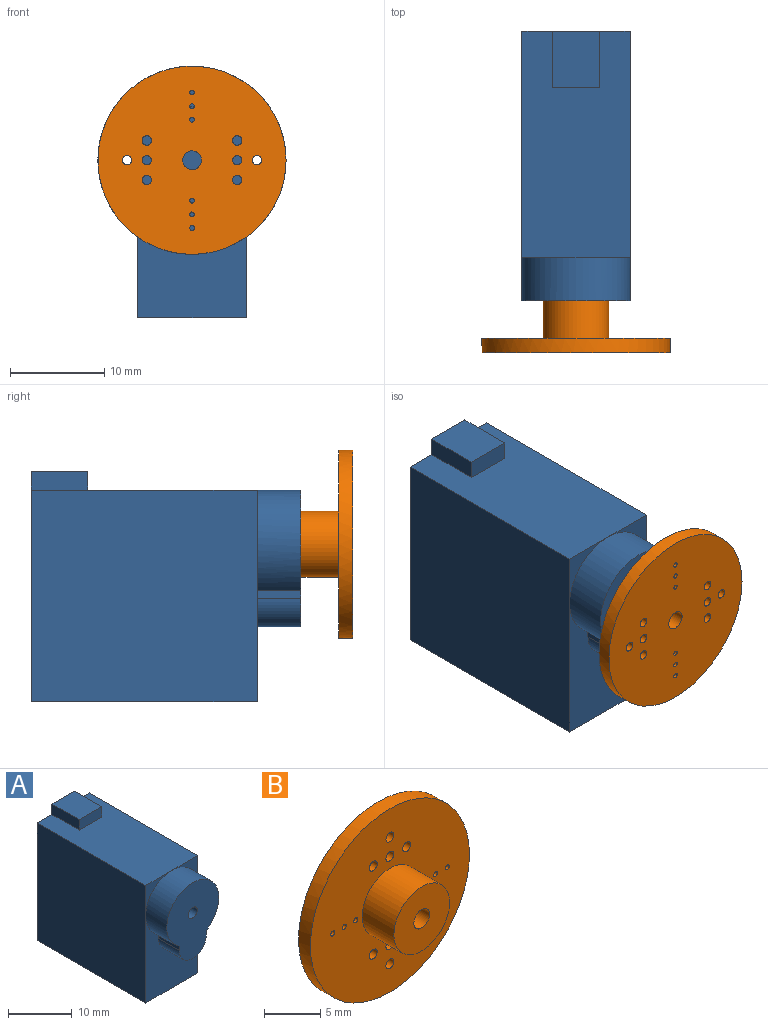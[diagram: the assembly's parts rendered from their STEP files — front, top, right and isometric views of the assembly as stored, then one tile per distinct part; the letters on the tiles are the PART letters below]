
ASSEMBLY  parts=2 mates=1
PART A: 27 faces, bbox 11.5x28.7x24.5 mm
  f0: plane 24x11.5mm, normal (0,0,1), area 246mm2, adj f1,f2,f4,f5,f7,f15,f16,f17
  f1: plane 5.75x5.75mm, normal (0,-1,0), area 7.1mm2, adj f0,f4,f11
  f2: plane 5.75x5.75mm, normal (0,-1,0), area 7.1mm2, adj f0,f5,f11
  f3: plane 16.75x11.5mm, normal (0,-1,0), area 124.9mm2, adj f4,f5,f6,f8,f9,f10,f11
  f4: plane 24x22.5mm, normal (1,0,0), area 540mm2, adj f0,f1,f3,f6,f7
  f5: plane 24x22.5mm, normal (-1,0,0), area 540mm2, adj f0,f2,f3,f6,f7
  f6: plane 24x11.5mm, normal (0,0,-1), area 276mm2, adj f3,f4,f5,f7
  f7: plane 24.5x11.5mm, normal (0,1,0), area 265.6mm2, adj f0,f4,f5,f6,f15,f16,f18,f19
  f8: plane 4.65x0.84mm, normal (-1,0,0), area 3.9mm2, adj f3,f9,f11,f12
  f9: cylinder r=3mm len=6mm, axis (0,1,0), area 43.8mm2, adj f3,f8,f10,f12
  f10: plane 4.65x0.84mm, normal (1,0,0), area 3.9mm2, adj f3,f9,f11,f12
  f11: cylinder r=5.75mm len=11.5mm, axis (0,1,0), area 138.6mm2, adj f1,f2,f3,f8,f10,f12
  f12: plane 14.5x11.5mm, normal (0,-1,0), area 116.5mm2, adj f8,f9,f10,f11,f13
  f13: cylinder r=1mm len=2mm, axis (0,-1,0), area 12.6mm2, adj f12,f14
  f14: plane 2x2mm, normal (0,-1,0), area 3.1mm2, adj f13
  f15: plane 6x2mm, normal (1,0,0), area 12mm2, adj f0,f7,f17,f18
  f16: plane 6x2mm, normal (-1,0,0), area 12mm2, adj f0,f7,f17,f18
  f17: plane 5x2mm, normal (0,-1,0), area 10mm2, adj f0,f15,f16,f18
  f18: plane 6x5mm, normal (0,0,1), area 30mm2, adj f7,f15,f16,f17
  f19: cylinder r=0.5mm len=1mm, axis (0,1,0), area 3.1mm2, adj f7,f20
  f20: plane 1x1mm, normal (0,1,0), area 0.8mm2, adj f19
  f21: cylinder r=0.5mm len=1mm, axis (0,1,0), area 3.1mm2, adj f7,f22
  f22: plane 1x1mm, normal (0,1,0), area 0.8mm2, adj f21
  f23: cylinder r=0.5mm len=1mm, axis (0,1,0), area 3.1mm2, adj f7,f24
  f24: plane 1x1mm, normal (0,1,0), area 0.8mm2, adj f23
  f25: cylinder r=0.5mm len=1mm, axis (0,1,0), area 3.1mm2, adj f7,f26
  f26: plane 1x1mm, normal (0,1,0), area 0.8mm2, adj f25
PART B: 20 faces, bbox 20x5.5x20 mm
  f0: plane 20x20mm, normal (0,-1,0), area 268.2mm2, adj f3,f4,f5,f6,f7,f8,f9,f10
  f1: plane 20x20mm, normal (0,1,0), area 303.6mm2, adj f2,f3,f4,f5,f6,f7,f8,f9
  f2: cylinder r=1mm len=5.5mm, axis (0,1,0), area 34.6mm2, adj f1,f18
  f3: cylinder r=0.5mm len=1.5mm, axis (0,1,0), area 4.7mm2, adj f0,f1
  f4: cylinder r=0.5mm len=1.5mm, axis (0,1,0), area 4.7mm2, adj f0,f1
  f5: cylinder r=0.5mm len=1.5mm, axis (0,1,0), area 4.7mm2, adj f0,f1
  f6: cylinder r=0.5mm len=1.5mm, axis (0,1,0), area 4.7mm2, adj f0,f1
  f7: cylinder r=0.5mm len=1.5mm, axis (0,1,0), area 4.7mm2, adj f0,f1
  f8: cylinder r=0.5mm len=1.5mm, axis (0,1,0), area 4.7mm2, adj f0,f1
  f9: cylinder r=0.5mm len=1.5mm, axis (0,1,0), area 4.7mm2, adj f0,f1
  f10: cylinder r=0.5mm len=1.5mm, axis (0,1,0), area 4.7mm2, adj f0,f1
  f11: cylinder r=0.25mm len=1.5mm, axis (0,1,0), area 2.4mm2, adj f0,f1
  f12: cylinder r=0.25mm len=1.5mm, axis (0,1,0), area 2.4mm2, adj f0,f1
  f13: cylinder r=0.25mm len=1.5mm, axis (0,1,0), area 2.4mm2, adj f0,f1
  f14: cylinder r=0.25mm len=1.5mm, axis (0,1,0), area 2.4mm2, adj f0,f1
  f15: cylinder r=0.25mm len=1.5mm, axis (0,1,0), area 2.4mm2, adj f0,f1
  f16: cylinder r=0.25mm len=1.5mm, axis (0,1,0), area 2.4mm2, adj f0,f1
  f17: cylinder r=10mm len=20mm, axis (0,1,0), area 94.2mm2, adj f0,f1
  f18: plane 7x7mm, normal (0,-1,0), area 35.3mm2, adj f2,f19
  f19: cylinder r=3.5mm len=7mm, axis (0,1,0), area 88mm2, adj f0,f18
PLACE A at identity fixed
PLACE B rot(axis=(0.71,0,0.71),180deg) t=(-12.5,1.15,-7.9)mm
MATE revolute B.f2 <-> A.f13  axis (0,1,0) through (0,-28.65,5.5)mm
